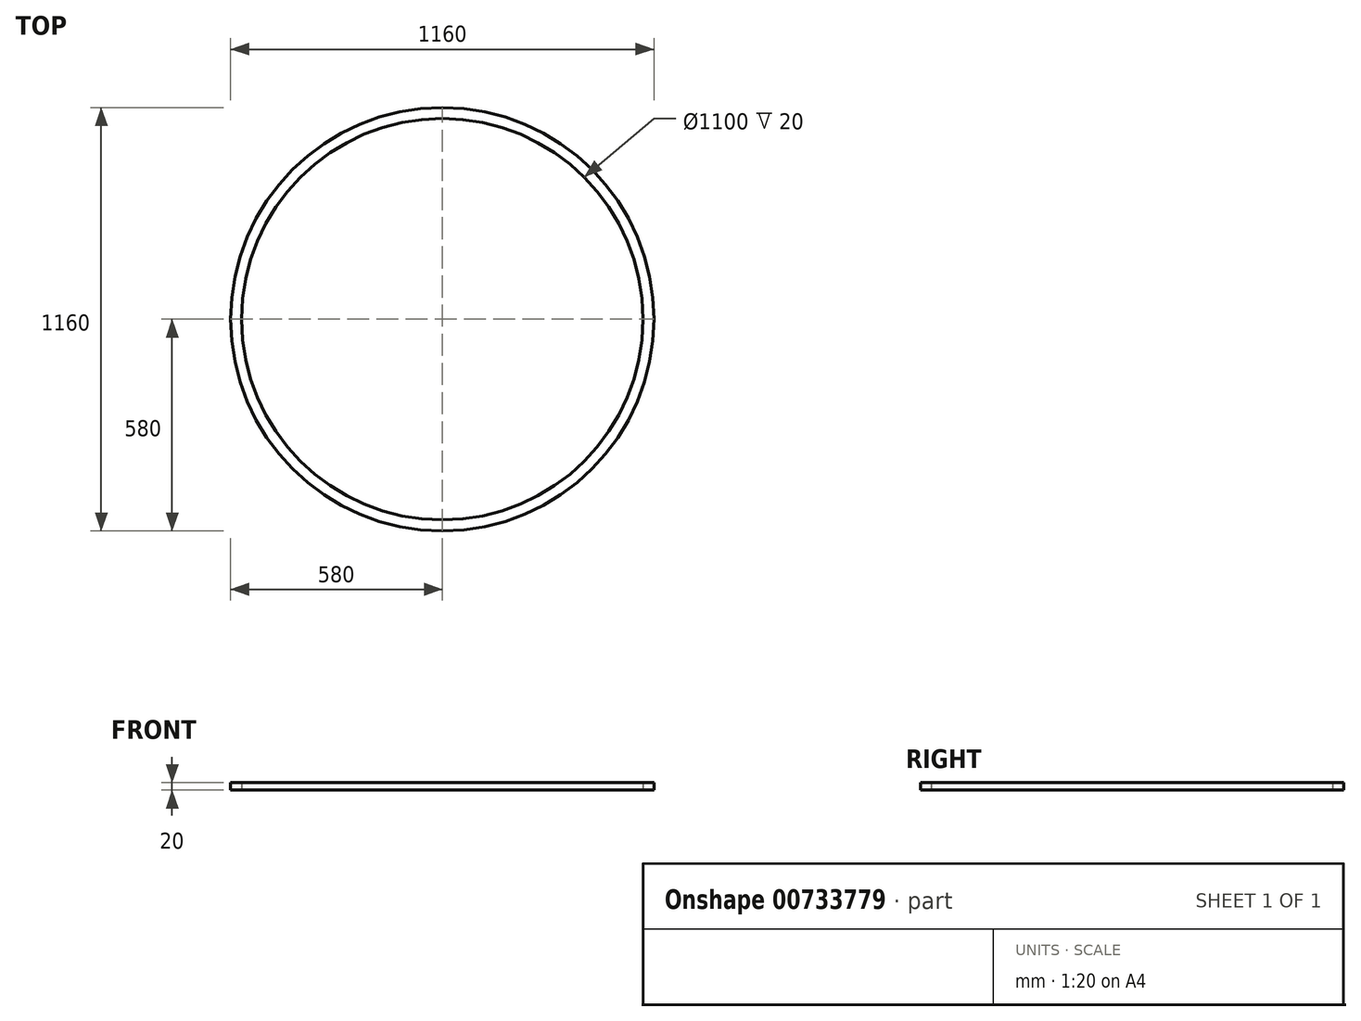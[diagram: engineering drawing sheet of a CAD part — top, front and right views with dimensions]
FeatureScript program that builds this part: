
annotation { "Feature Type Name" : "Feature", "Feature Type Description" : "" }
export const myFeature = defineFeature(function(context is Context, id is Id, definition is map)
    precondition{}
    {
        {
            var Q0;
            Q0=qCreatedBy(makeId("Top.planeOp"),FACE);
            var sketch = newSketch(context, id + "F0", { "sketchPlane" : qUnion([Q0])});
            skCircle(sketch, "E0", {"center": v(0, 0) * mm, "radius": 580 * mm});
            skCircle(sketch, "E1.0", {"center": v(0, 0) * mm, "radius": 550 * mm});
            skSolve(sketch);
        }
        {
            var Q0;
            Q0=qSketchRegion(id+"F0",true);
            extrude(context, id + "F1", {"entities" : qUnion([Q0]), "depth" : 20 * mm, "offsetDistance" : 25 * mm});
        }
    });
